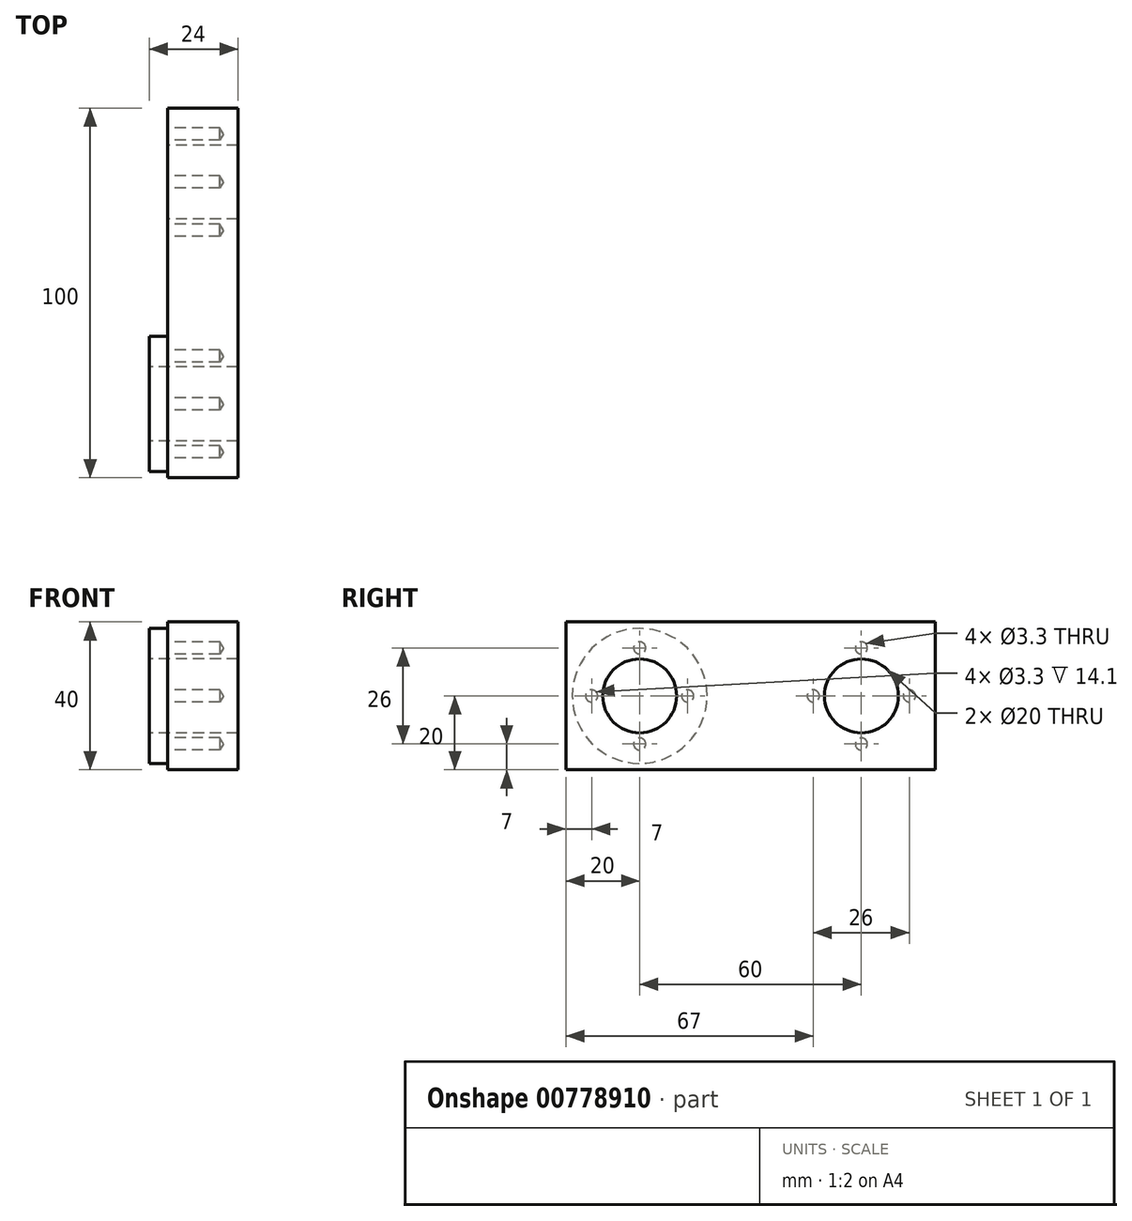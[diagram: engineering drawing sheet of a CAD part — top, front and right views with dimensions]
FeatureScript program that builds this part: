
annotation { "Feature Type Name" : "Feature", "Feature Type Description" : "" }
export const myFeature = defineFeature(function(context is Context, id is Id, definition is map)
    precondition{}
    {
        {
            var Q0;
            Q0=qCreatedBy(makeId("Right.planeOp"),FACE);
            var sketch = newSketch(context, id + "F0", { "sketchPlane" : qUnion([Q0])});
            skLineSegment(sketch, "E0.bottom", {"start": v(50, -20) * mm, "end": v(-50, -20) * mm});
            skLineSegment(sketch, "E0.top", {"start": v(50, 20) * mm, "end": v(-50, 20) * mm});
            skLineSegment(sketch, "E0.left", {"start": v(50, -20) * mm, "end": v(50, 20) * mm});
            skLineSegment(sketch, "E0.right", {"start": v(-50, -20) * mm, "end": v(-50, 20) * mm});
            skPoint(sketch, "E0.middle", {"position": v(0, 0) * mm});
            skPoint(sketch, "E1", {"position": v(-30, 0) * mm});
            skCircle(sketch, "E2", {"center": v(-30, 0) * mm, "radius": 10 * mm});
            skCircle(sketch, "E3.MirrorC", {"center": v(30, 0) * mm, "radius": 10 * mm});
            skSolve(sketch);
        }
        {
            var Q0;
            Q0=makeQuery(id+"F0.imprint","IMPRINT",FACE,{"disambiguationData":[TD([[makeQuery(id+"F0.imprint","IMPRINT",EDGE,{"derivedFrom":sQuery(id+"F0.wireOp",EDGE,"E0.bottom")}),-1.0]])]});
            extrude(context, id + "F1", {"entities" : qUnion([Q0]), "depth" : 24 * mm, "offsetDistance" : 25 * mm});
        }
        {
            var Q0;
            Q0=makeQuery(id+"F1.opExtrude","CAP_FACE",FACE,{"disambiguationData":[OSD([sQuery(id+"F0.wireOp",EDGE,"E0.bottom"),sQuery(id+"F0.wireOp",EDGE,"E0.top"),sQuery(id+"F0.wireOp",EDGE,"E0.left"),sQuery(id+"F0.wireOp",EDGE,"E0.right"),sQuery(id+"F0.wireOp",EDGE,"E2"),sQuery(id+"F0.wireOp",EDGE,"E3.MirrorC")])],"isStart":true});
            var sketch = newSketch(context, id + "F2", { "sketchPlane" : qUnion([Q0])});
            skCircle(sketch, "E4", {"center": v(-30, 0) * mm, "radius": 18.25 * mm});
            skCircle(sketch, "E5.MirrorC", {"center": v(30, 0) * mm, "radius": 18.25 * mm});
            skSolve(sketch);
        }
        {
            var Q0;
            Q0=makeQuery(id+"F2.imprint","IMPRINT",FACE,{"disambiguationData":[TD([[makeQuery(id+"F2.imprint","IMPRINT",EDGE,{"derivedFrom":sQuery(id+"F2.wireOp",EDGE,"E4")}),1.0]])]});
            var Q1;
            Q1=makeQuery(id+"F2.imprint","IMPRINT",FACE,{"disambiguationData":[TD([[makeQuery(id+"F2.imprint","IMPRINT",EDGE,{"derivedFrom":sQuery(id+"F2.wireOp",EDGE,"E5.MirrorC")}),-1.0]])]});
            extrude(context, id + "F3", {"entities" : qUnion([Q0, Q1]), "operationType" : NewBodyOperationType.REMOVE, "oppositeDirection" : true, "depth" : 5 * mm, "offsetDistance" : 25 * mm});
        }
        {
            var Q0;
            Q0=makeQuery(id+"F3.boolean.opBoolean","COPY",FACE,{"derivedFrom":makeQuery(id+"F3.opExtrude","CAP_FACE",FACE,{"disambiguationData":[OSD([sQuery(id+"F0.wireOp",EDGE,"E3.MirrorC"),sQuery(id+"F2.wireOp",EDGE,"E4")])],"isStart":false})});
            var sketch = newSketch(context, id + "F4", { "sketchPlane" : qUnion([Q0])});
            skPoint(sketch, "E6", {"position": v(-43, 0) * mm});
            skPoint(sketch, "E7", {"position": v(-30, 0) * mm});
            skCircle(sketch, "E8", {"center": v(-30, 0) * mm, "radius": 13 * mm, "construction": true});
            skPoint(sketch, "E9", {"position": v(-30, 13) * mm});
            skPoint(sketch, "E10", {"position": v(-17, 0) * mm});
            skPoint(sketch, "E11", {"position": v(-30, -13) * mm});
            skCircle(sketch, "E12.MirrorC", {"center": v(30, 0) * mm, "radius": 13 * mm, "construction": true});
            skPoint(sketch, "E13.MirrorP", {"position": v(43, 0) * mm});
            skPoint(sketch, "E14.MirrorP", {"position": v(30, 13) * mm});
            skPoint(sketch, "E15.MirrorP", {"position": v(17, 0) * mm});
            skPoint(sketch, "E16.MirrorP", {"position": v(30, -13) * mm});
            skSolve(sketch);
        }
        {
            var Q0;
            Q0=sQuery(id+"F4.wireOp",VERTEX,"E6");
            var Q1;
            Q1=sQuery(id+"F4.wireOp",VERTEX,"E9");
            var Q2;
            Q2=sQuery(id+"F4.wireOp",VERTEX,"E10");
            var Q3;
            Q3=sQuery(id+"F4.wireOp",VERTEX,"E11");
            var Q4;
            Q4=sQuery(id+"F4.wireOp",VERTEX,"E15.MirrorP");
            var Q5;
            Q5=sQuery(id+"F4.wireOp",VERTEX,"E14.MirrorP");
            var Q6;
            Q6=sQuery(id+"F4.wireOp",VERTEX,"E13.MirrorP");
            var Q7;
            Q7=sQuery(id+"F4.wireOp",VERTEX,"E16.MirrorP");
            var Q8;
            Q8=makeQuery(id+"F1.opExtrude","SWEPT_BODY",BODY,{"disambiguationData":[OSD([sQuery(id+"F0.wireOp",EDGE,"E0.bottom"),sQuery(id+"F0.wireOp",EDGE,"E0.top"),sQuery(id+"F0.wireOp",EDGE,"E0.left"),sQuery(id+"F0.wireOp",EDGE,"E0.right"),sQuery(id+"F0.wireOp",EDGE,"E2"),sQuery(id+"F0.wireOp",EDGE,"E3.MirrorC")])]});
            hole(context, id + "F5", {"style" : HoleStyle.SIMPLE, "endStyle" : HoleEndStyle.BLIND, "standardTappedOrClearance" : lookupTablePath({ "standard" : "ISO", "engagement" : "75%", "pitch" : "0.7 mm", "size" : "M4", "type" : "Tapped" }), "standardBlindInLast" : lookupTablePath({ "standard" : "ISO", "engagement" : "75%", "pitch" : "0.7 mm", "size" : "M4", "type" : "Tapped" }), "holeDiameter" : 3.3 * mm, "majorDiameter" : 4 * mm, "showTappedDepth" : true, "holeDepth" : 14.1 * mm, "tappedDepth" : 12 * mm, "tapClearance" : 3, "locations" : qUnion([Q0, Q1, Q2, Q3, Q4, Q5, Q6, Q7]), "scope" : qUnion([Q8])});
        }
    });
